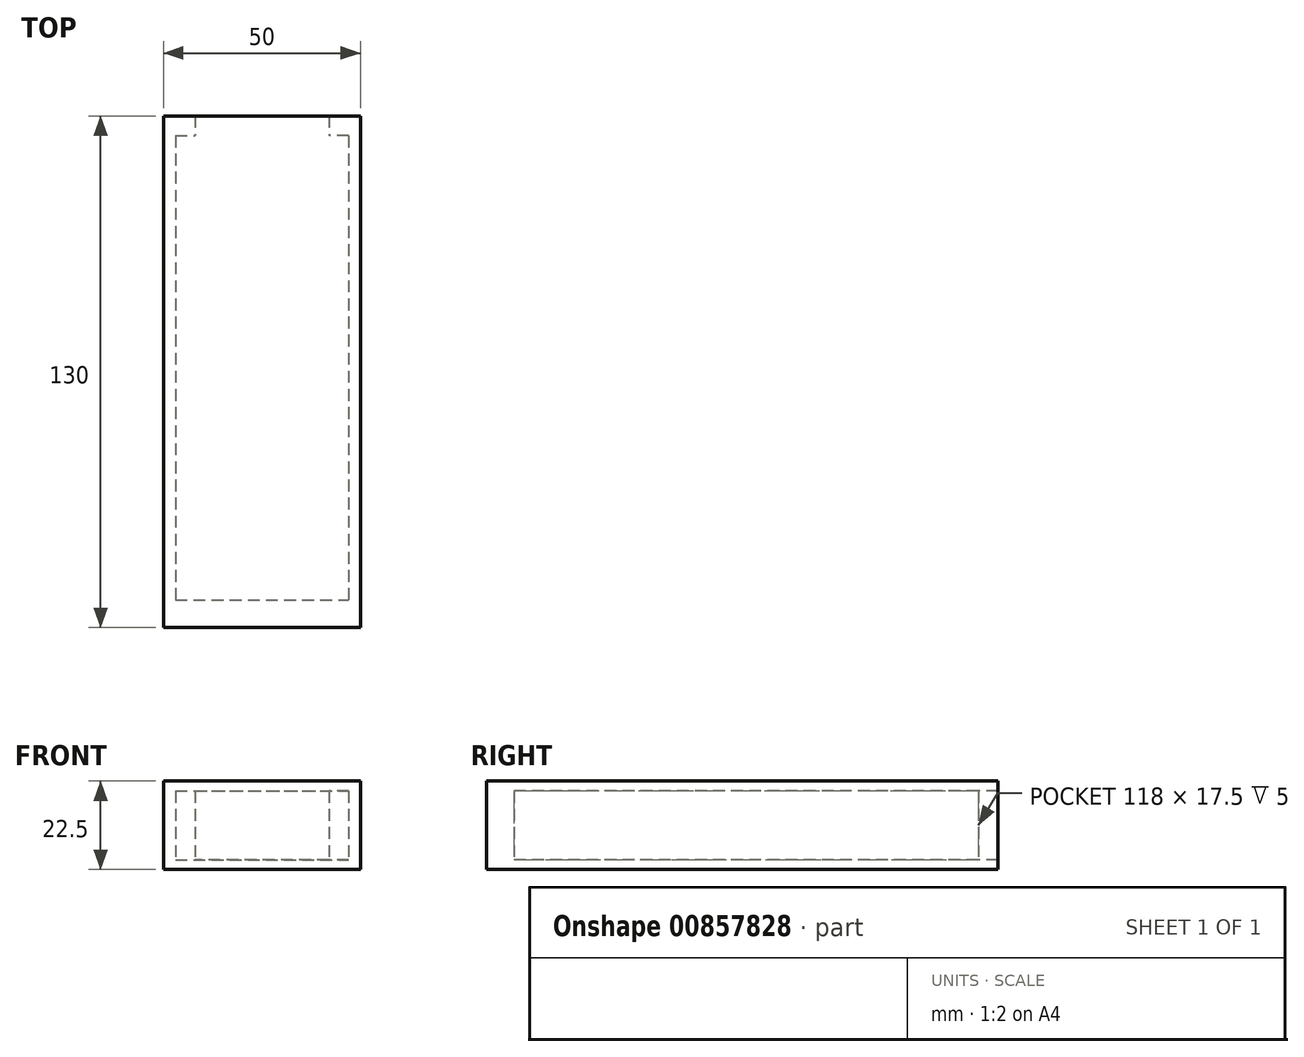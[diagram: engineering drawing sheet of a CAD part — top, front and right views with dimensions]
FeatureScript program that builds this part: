
annotation { "Feature Type Name" : "Feature", "Feature Type Description" : "" }
export const myFeature = defineFeature(function(context is Context, id is Id, definition is map)
    precondition{}
    {
        {
            var Q0;
            Q0=qCreatedBy(makeId("Top.planeOp"),FACE);
            var sketch = newSketch(context, id + "F0", { "sketchPlane" : qUnion([Q0])});
            skLineSegment(sketch, "E0.bottom", {"start": v(25, 65) * mm, "end": v(-25, 65) * mm});
            skLineSegment(sketch, "E0.top", {"start": v(25, -65) * mm, "end": v(-25, -65) * mm});
            skLineSegment(sketch, "E0.left", {"start": v(25, 65) * mm, "end": v(25, -65) * mm});
            skLineSegment(sketch, "E0.right", {"start": v(-25, 65) * mm, "end": v(-25, -65) * mm});
            skPoint(sketch, "E0.middle", {"position": v(0, 0) * mm});
            skLineSegment(sketch, "E1.0", {"start": v(-22, 65) * mm, "end": v(-22, -58) * mm});
            skLineSegment(sketch, "E1.2", {"start": v(22, 65) * mm, "end": v(22, -58) * mm});
            skLineSegment(sketch, "E2", {"start": v(-22, -58) * mm, "end": v(22, -58) * mm});
            skLineSegment(sketch, "E3.bottom", {"start": v(-22, 65) * mm, "end": v(-17, 65) * mm});
            skLineSegment(sketch, "E3.top", {"start": v(-22, 60) * mm, "end": v(-17, 60) * mm});
            skLineSegment(sketch, "E3.left", {"start": v(-22, 65) * mm, "end": v(-22, 60) * mm});
            skLineSegment(sketch, "E3.right", {"start": v(-17, 65) * mm, "end": v(-17, 60) * mm});
            skLineSegment(sketch, "E4.bottom", {"start": v(22, 65) * mm, "end": v(17, 65) * mm});
            skLineSegment(sketch, "E4.top", {"start": v(22, 60) * mm, "end": v(17, 60) * mm});
            skLineSegment(sketch, "E4.left", {"start": v(22, 65) * mm, "end": v(22, 60) * mm});
            skLineSegment(sketch, "E4.right", {"start": v(17, 65) * mm, "end": v(17, 60) * mm});
            skSolve(sketch);
        }
        {
            var Q0;
            {var subQ0=sQuery(id+"F0.wireOp",EDGE,"E2");Q0=makeQuery(id+"F0.imprint","IMPRINT",FACE,{"disambiguationData":[TD([[makeQuery(id+"F0.imprint","IMPRINT",EDGE,{"derivedFrom":subQ0}),1.0]])]});}
            extrude(context, id + "F1", {"entities" : qUnion([Q0]), "depth" : 2.5 * mm, "offsetDistance" : 25 * mm});
        }
        {
            var Q0;
            {var subQ4=sQuery(id+"F0.wireOp",EDGE,"E4.top");Q0=makeQuery(id+"F0.imprint","IMPRINT",FACE,{"disambiguationData":[TD([[makeQuery(id+"F0.imprint","IMPRINT",EDGE,{"derivedFrom":subQ4}),-1.0]])]});}
            var Q1;
            Q1=makeQuery(id+"F0.imprint","IMPRINT",FACE,{"disambiguationData":[TD([[makeQuery(id+"F0.imprint","IMPRINT",EDGE,{"derivedFrom":sQuery(id+"F0.wireOp",EDGE,"E0.top")}),-1.0]])]});
            var Q2;
            {var subQ4=sQuery(id+"F0.wireOp",EDGE,"E3.top");Q2=makeQuery(id+"F0.imprint","IMPRINT",FACE,{"disambiguationData":[TD([[makeQuery(id+"F0.imprint","IMPRINT",EDGE,{"derivedFrom":subQ4}),1.0]])]});}
            extrude(context, id + "F2", {"entities" : qUnion([Q0, Q1, Q2]), "operationType" : NewBodyOperationType.ADD, "depth" : 20 * mm, "offsetDistance" : 25 * mm});
        }
        {
            var Q0;
            Q0=makeQuery(id+"F2.opExtrude","CAP_FACE",FACE,{"disambiguationData":[OSD([sQuery(id+"F0.wireOp",EDGE,"E0.bottom"),sQuery(id+"F0.wireOp",EDGE,"E0.top"),sQuery(id+"F0.wireOp",EDGE,"E0.left"),sQuery(id+"F0.wireOp",EDGE,"E0.right"),sQuery(id+"F0.wireOp",EDGE,"E1.0"),sQuery(id+"F0.wireOp",EDGE,"E1.2"),sQuery(id+"F0.wireOp",EDGE,"E2"),sQuery(id+"F0.wireOp",EDGE,"E3.top"),sQuery(id+"F0.wireOp",EDGE,"E3.right"),sQuery(id+"F0.wireOp",EDGE,"E4.top"),sQuery(id+"F0.wireOp",EDGE,"E4.right")])],"isStart":false});
            var sketch = newSketch(context, id + "F3", { "sketchPlane" : qUnion([Q0])});
            skLineSegment(sketch, "E5.bottom", {"start": v(-25, 65) * mm, "end": v(25, 65) * mm});
            skLineSegment(sketch, "E5.top", {"start": v(-25, -65) * mm, "end": v(25, -65) * mm});
            skLineSegment(sketch, "E5.left", {"start": v(-25, 65) * mm, "end": v(-25, -65) * mm});
            skLineSegment(sketch, "E5.right", {"start": v(25, 65) * mm, "end": v(25, -65) * mm});
            skSolve(sketch);
        }
        {
            var Q0;
            Q0 = qSketchRegion(id + "F3", true);
            extrude(context, id + "F4", {"entities" : qUnion([Q0]), "operationType" : NewBodyOperationType.ADD, "depth" : 2.5 * mm, "offsetDistance" : 25 * mm});
        }
    });
